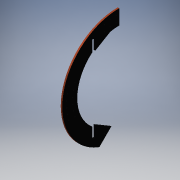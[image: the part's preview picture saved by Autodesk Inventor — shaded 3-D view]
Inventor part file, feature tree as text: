
AUTODESK INVENTOR PART (.ipt)
format: ipt  version: 2016 (Build 200138000, 138)  size: 229,376 bytes
history: native  units: in
note: dims shown in document units (in); Inventor stores cm internally (conversion verified against a paired STEP export)
features: extrude x3, sketch x3, reference x3
ambient origin geometry x8: Origin, YZ Plane, XZ Plane, XY Plane, X Axis, Y Axis, Z Axis, Center Point
bodies: Solid1 (feature_tree)
feature tree (9):
  extrude  "Extrusion1"  Depth=14.0in
  extrude  "Extrusion2"  Depth=0.25in
  extrude  "Extrusion3"  Depth=0.25in
  sketch  "Sketch1"  dims[d0=19.0in d1=14.0in]
  sketch  "Sketch2"  dims[d2=0.25in d3=17.5in]
  reference  "Reference1"
  sketch  "Sketch3"  dims[d4=0.25in d5=0.25in d6=1.0in d7=1.0in d8=15.5in d9=0.25in d10=0.25in d11=0.25in d13=0.5in d14=0.5in d15=1.0in d16=1.0in d17=45.0deg d18=45.0deg d19=0.25in d20=0.0in d21=1.0in d22=0.0in d23=0.25in d24=0.0in]
  reference  "Reference2"
  reference  "Reference3"
